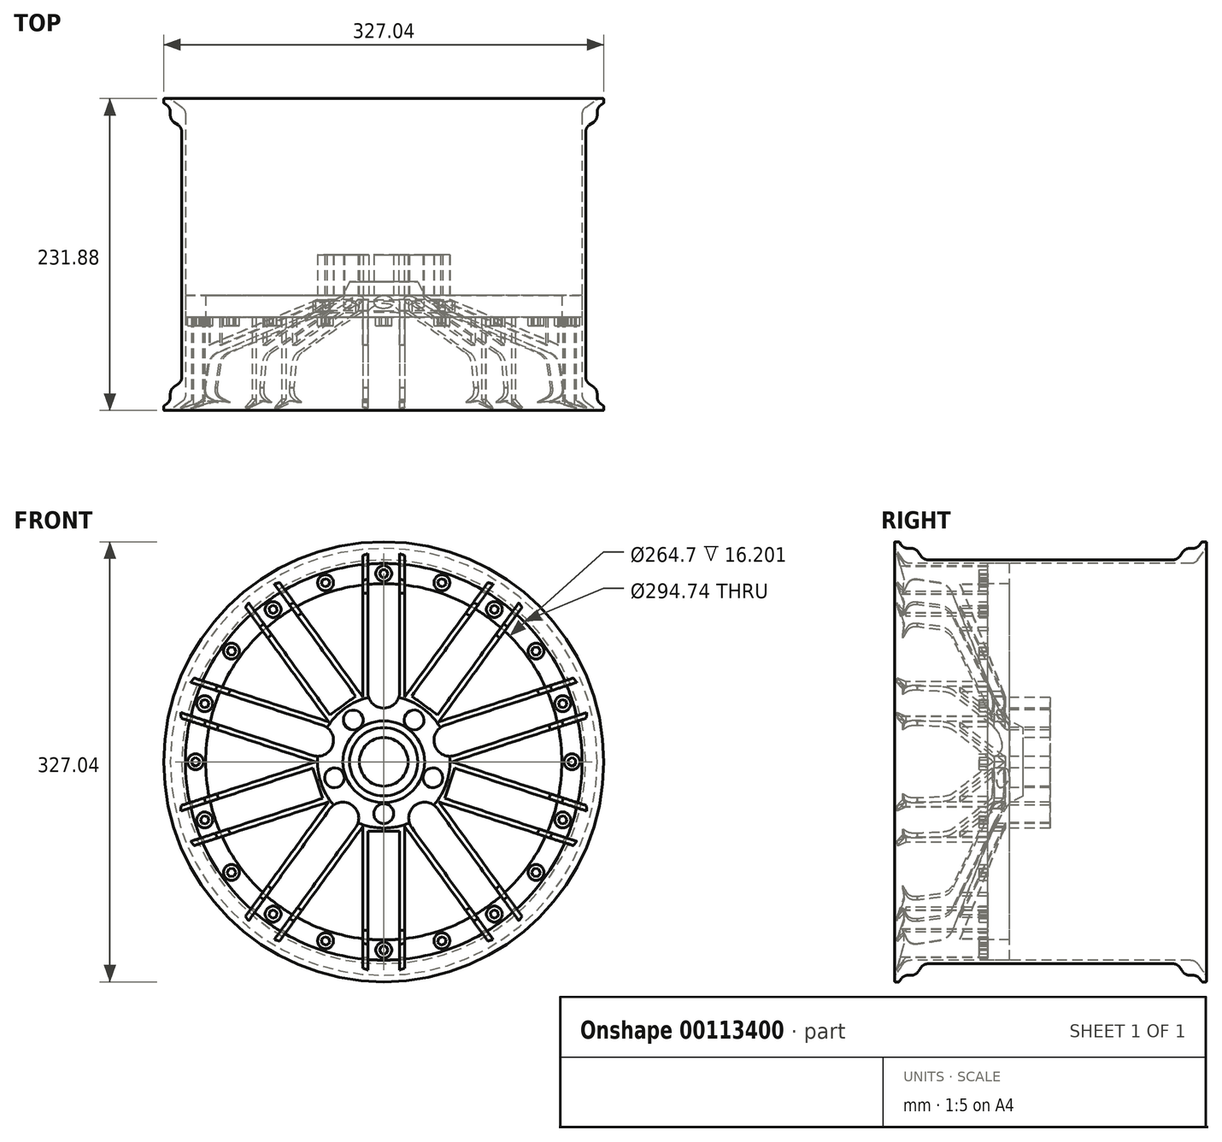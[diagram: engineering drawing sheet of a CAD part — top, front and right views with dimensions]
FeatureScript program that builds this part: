
annotation { "Feature Type Name" : "Feature", "Feature Type Description" : "" }
export const myFeature = defineFeature(function(context is Context, id is Id, definition is map)
    precondition{}
    {
        {
            var Q0;
            Q0=qCreatedBy(makeId("Right.planeOp"),FACE);
            var sketch = newSketch(context, id + "F0", { "sketchPlane" : qUnion([Q0])});
            skLineSegment(sketch, "E0", {"start": v(0, 0) * mm, "end": v(0, 25.37) * mm});
            skLineSegment(sketch, "E1", {"start": v(0, 25.37) * mm, "end": v(-9.97, 30.36) * mm});
            skLineSegment(sketch, "E2", {"start": v(-9.97, 30.36) * mm, "end": v(-21.68, 49.22) * mm});
            skLineSegment(sketch, "E3", {"start": v(-21.68, 49.22) * mm, "end": v(-52.6, 125.8) * mm});
            skLineSegment(sketch, "E4", {"start": v(-62.4, 133.6) * mm, "end": v(-78.7, 136.17) * mm});
            skLineSegment(sketch, "E5", {"start": v(-78.7, 136.17) * mm, "end": v(-80.6, 136.17) * mm});
            skLineSegment(sketch, "E6", {"start": v(-86.3, 132.6) * mm, "end": v(-89.55, 125.98) * mm});
            skLineSegment(sketch, "E7", {"start": v(-89.55, 125.98) * mm, "end": v(-88.47, 135.95) * mm});
            skLineSegment(sketch, "E8", {"start": v(-46.84, 132.48) * mm, "end": v(-13.23, 49.22) * mm});
            skLineSegment(sketch, "E9", {"start": v(-13.23, 49.22) * mm, "end": v(19.95, 49.22) * mm});
            skLineSegment(sketch, "E10", {"start": v(19.95, 49.22) * mm, "end": v(19.95, 0) * mm});
            skLineSegment(sketch, "E11", {"start": v(19.95, 0) * mm, "end": v(0, 0) * mm});
            skLineSegment(sketch, "E12", {"start": v(-46.84, 132.48) * mm, "end": v(-26.45, 132.48) * mm});
            skLineSegment(sketch, "E13", {"start": v(-26.45, 132.48) * mm, "end": v(-26.45, 145.93) * mm});
            skLineSegment(sketch, "E14", {"start": v(-26.45, 145.93) * mm, "end": v(-87.38, 145.93) * mm});
            skLineSegment(sketch, "E15", {"start": v(-40.33, 0) * mm, "end": v(58.54, 0) * mm});
            skLineSegment(sketch, "E16", {"start": v(-94.12, 155.55) * mm, "end": v(-88.47, 135.95) * mm});
            skLineSegment(sketch, "E17", {"start": v(-94.12, 155.55) * mm, "end": v(-87.38, 145.93) * mm});
            skPoint(sketch, "E18.visualSharp", {"position": v(-55.3, 132.48) * mm});
            skArc(sketch, "E18.filletArc", {"start": v(-55.17, 132.18) * mm, "mid": v(-55.35, 132.41) * mm, "end": v(-55.62, 132.53) * mm});
            skArc(sketch, "E19.filletArc", {"start": v(-52.6, 125.8) * mm, "mid": v(-56.47, 131) * mm, "end": v(-62.4, 133.6) * mm});
            skPoint(sketch, "E20.visualSharp", {"position": v(-84.56, 136.17) * mm});
            skArc(sketch, "E20.filletArc", {"start": v(-80.6, 136.17) * mm, "mid": v(-83.96, 135.2) * mm, "end": v(-86.3, 132.6) * mm});
            skSolve(sketch);
        }
        {
            var Q0;
            Q0 = qSketchRegion(id + "F0", true);
            var Q1;
            Q1=sQuery(id+"F0.wireOp",EDGE,"E15");
            revolve(context, id + "F1", {"entities" : qUnion([Q0]), "axis" : qUnion([Q1]), "revolveType" : RevolveType.FULL});
        }
        {
            var Q0;
            Q0=makeQuery(id+"F1.opRevolve","SWEPT_FACE",FACE,{"disambiguationData":[OSD([sQuery(id+"F0.wireOp",EDGE,"E0")])]});
            cPlane(context, id + "F2", {"entities" : qUnion([Q0]), "cplaneType" : CPlaneType.OFFSET, "offset" : 94.13 * mm, "width" : 152.4 * mm, "height" : 152.4 * mm});
        }
        {
            var Q0;
            Q0=qCreatedBy(id+"F2.planeOp",FACE);
            var sketch = newSketch(context, id + "F3", { "sketchPlane" : qUnion([Q0])});
            skCircle(sketch, "E21.cCircle", {"center": v(0, 0) * mm, "radius": 31.14 * mm, "construction": true});
            skPoint(sketch, "E21.0.midPoint", {"position": v(0, 31.14) * mm});
            skCircle(sketch, "E22", {"center": v(-22.63, 31.14) * mm, "radius": 7.35 * mm});
            skCircle(sketch, "E23", {"center": v(22.63, 31.14) * mm, "radius": 7.35 * mm});
            skCircle(sketch, "E24", {"center": v(36.61, -11.9) * mm, "radius": 7.35 * mm});
            skCircle(sketch, "E25", {"center": v(0, -38.5) * mm, "radius": 7.35 * mm});
            skCircle(sketch, "E26", {"center": v(-36.61, -11.9) * mm, "radius": 7.35 * mm});
            skCircle(sketch, "E27", {"center": v(0, 0) * mm, "radius": 18.07 * mm});
            skCircle(sketch, "E28.cCircle", {"center": v(0, 0) * mm, "radius": 48.17 * mm, "construction": true});
            skPoint(sketch, "E28.0.midPoint", {"position": v(0, -48.17) * mm});
            skLineSegment(sketch, "E29.left", {"start": v(15.65, -48.17) * mm, "end": v(15.65, -143.7) * mm});
            skLineSegment(sketch, "E29.right", {"start": v(-15.65, -48.17) * mm, "end": v(-15.65, -143.7) * mm});
            skLineSegment(sketch, "E30.bottom", {"start": v(11.83, -51.7) * mm, "end": v(-11.84, -51.7) * mm});
            skLineSegment(sketch, "E30.left", {"start": v(11.83, -51.7) * mm, "end": v(11.83, -145.13) * mm});
            skLineSegment(sketch, "E30.right", {"start": v(-11.84, -51.7) * mm, "end": v(-11.84, -145.13) * mm});
            skLineSegment(sketch, "E31.MirrorCS", {"start": v(-11.83, -145.13) * mm, "end": v(-11.84, -145.13) * mm});
            skPoint(sketch, "E32.orphan", {"position": v(-15.65, -149.28) * mm});
            skLineSegment(sketch, "E33.1.0", {"start": v(39.96, -34.87) * mm, "end": v(94.88, -110.46) * mm});
            skLineSegment(sketch, "E33.1.1", {"start": v(40.97, -29.77) * mm, "end": v(97.13, -107.06) * mm});
            skLineSegment(sketch, "E33.1.3", {"start": v(39.96, -34.87) * mm, "end": v(39.95, -34.87) * mm});
            skLineSegment(sketch, "E33.1.4", {"start": v(20.8, -48.78) * mm, "end": v(75.73, -124.37) * mm});
            skLineSegment(sketch, "E33.1.5", {"start": v(15.65, -48.17) * mm, "end": v(71.8, -125.46) * mm});
            skLineSegment(sketch, "E33.1.6", {"start": v(75.74, -124.37) * mm, "end": v(75.73, -124.37) * mm});
            skLineSegment(sketch, "E33.2.0", {"start": v(52.82, -4.72) * mm, "end": v(141.69, -33.6) * mm});
            skLineSegment(sketch, "E33.2.1", {"start": v(50.65, 0) * mm, "end": v(141.5, -29.52) * mm});
            skLineSegment(sketch, "E33.2.3", {"start": v(52.82, -4.72) * mm, "end": v(45.5, -27.23) * mm});
            skLineSegment(sketch, "E33.2.4", {"start": v(45.5, -27.23) * mm, "end": v(134.37, -56.1) * mm});
            skLineSegment(sketch, "E33.2.5", {"start": v(40.97, -29.77) * mm, "end": v(131.83, -59.3) * mm});
            skLineSegment(sketch, "E33.2.6", {"start": v(134.37, -56.1) * mm, "end": v(134.37, -56.1) * mm});
            skLineSegment(sketch, "E33.3.0", {"start": v(45.51, 27.23) * mm, "end": v(134.37, 56.1) * mm});
            skLineSegment(sketch, "E33.3.1", {"start": v(40.97, 29.77) * mm, "end": v(131.83, 59.3) * mm});
            skLineSegment(sketch, "E33.3.4", {"start": v(52.82, 4.72) * mm, "end": v(141.69, 33.59) * mm});
            skLineSegment(sketch, "E33.3.5", {"start": v(50.65, 0) * mm, "end": v(141.5, 29.52) * mm});
            skLineSegment(sketch, "E33.3.6", {"start": v(141.69, 33.6) * mm, "end": v(141.69, 33.59) * mm});
            skLineSegment(sketch, "E33.4.0", {"start": v(20.82, 48.78) * mm, "end": v(75.74, 124.37) * mm});
            skLineSegment(sketch, "E33.4.1", {"start": v(15.65, 48.17) * mm, "end": v(71.8, 125.46) * mm});
            skLineSegment(sketch, "E33.4.3", {"start": v(20.82, 48.78) * mm, "end": v(39.96, 34.87) * mm});
            skLineSegment(sketch, "E33.4.4", {"start": v(39.96, 34.87) * mm, "end": v(94.88, 110.46) * mm});
            skLineSegment(sketch, "E33.4.5", {"start": v(40.97, 29.77) * mm, "end": v(97.13, 107.06) * mm});
            skLineSegment(sketch, "E33.4.6", {"start": v(94.88, 110.46) * mm, "end": v(94.88, 110.46) * mm});
            skLineSegment(sketch, "E33.5.0", {"start": v(-11.83, 51.7) * mm, "end": v(-11.83, 145.13) * mm});
            skLineSegment(sketch, "E33.5.1", {"start": v(-15.65, 48.17) * mm, "end": v(-15.65, 143.7) * mm});
            skLineSegment(sketch, "E33.5.4", {"start": v(11.84, 51.7) * mm, "end": v(11.84, 145.13) * mm});
            skLineSegment(sketch, "E33.5.5", {"start": v(15.65, 48.17) * mm, "end": v(15.65, 143.7) * mm});
            skLineSegment(sketch, "E33.5.6", {"start": v(11.83, 145.13) * mm, "end": v(11.84, 145.13) * mm});
            skLineSegment(sketch, "E33.6.0", {"start": v(-39.96, 34.87) * mm, "end": v(-94.88, 110.46) * mm});
            skLineSegment(sketch, "E33.6.1", {"start": v(-40.97, 29.77) * mm, "end": v(-97.13, 107.06) * mm});
            skLineSegment(sketch, "E33.6.3", {"start": v(-39.96, 34.87) * mm, "end": v(-20.8, 48.78) * mm});
            skLineSegment(sketch, "E33.6.4", {"start": v(-20.8, 48.78) * mm, "end": v(-75.73, 124.37) * mm});
            skLineSegment(sketch, "E33.6.5", {"start": v(-15.65, 48.17) * mm, "end": v(-71.8, 125.46) * mm});
            skLineSegment(sketch, "E33.6.6", {"start": v(-75.74, 124.37) * mm, "end": v(-75.73, 124.37) * mm});
            skLineSegment(sketch, "E33.7.0", {"start": v(-52.82, 4.72) * mm, "end": v(-141.69, 33.6) * mm});
            skLineSegment(sketch, "E33.7.1", {"start": v(-50.65, 0) * mm, "end": v(-141.5, 29.52) * mm});
            skLineSegment(sketch, "E33.7.4", {"start": v(-45.5, 27.23) * mm, "end": v(-134.37, 56.1) * mm});
            skLineSegment(sketch, "E33.7.5", {"start": v(-40.97, 29.77) * mm, "end": v(-131.83, 59.3) * mm});
            skLineSegment(sketch, "E33.7.6", {"start": v(-134.37, 56.1) * mm, "end": v(-134.37, 56.1) * mm});
            skLineSegment(sketch, "E33.8.0", {"start": v(-45.51, -27.23) * mm, "end": v(-134.37, -56.1) * mm});
            skLineSegment(sketch, "E33.8.1", {"start": v(-40.97, -29.77) * mm, "end": v(-131.83, -59.3) * mm});
            skLineSegment(sketch, "E33.8.3", {"start": v(-45.51, -27.23) * mm, "end": v(-52.82, -4.72) * mm});
            skLineSegment(sketch, "E33.8.4", {"start": v(-52.82, -4.72) * mm, "end": v(-141.69, -33.59) * mm});
            skLineSegment(sketch, "E33.8.5", {"start": v(-50.65, 0) * mm, "end": v(-141.5, -29.52) * mm});
            skLineSegment(sketch, "E33.8.6", {"start": v(-141.69, -33.6) * mm, "end": v(-141.69, -33.59) * mm});
            skLineSegment(sketch, "E33.9.0", {"start": v(-20.82, -48.78) * mm, "end": v(-75.74, -124.37) * mm});
            skLineSegment(sketch, "E33.9.1", {"start": v(-15.65, -48.17) * mm, "end": v(-71.8, -125.46) * mm});
            skLineSegment(sketch, "E33.9.4", {"start": v(-39.96, -34.87) * mm, "end": v(-94.88, -110.46) * mm});
            skLineSegment(sketch, "E33.9.5", {"start": v(-40.97, -29.77) * mm, "end": v(-97.13, -107.06) * mm});
            skLineSegment(sketch, "E33.9.6", {"start": v(-94.88, -110.46) * mm, "end": v(-94.88, -110.46) * mm});
            skPoint(sketch, "E34.orphan", {"position": v(40.97, -29.77) * mm});
            skPoint(sketch, "E35.orphan", {"position": v(-15.65, -48.17) * mm});
            skPoint(sketch, "E36.orphan", {"position": v(-40.97, -29.77) * mm});
            skPoint(sketch, "E37.orphan", {"position": v(-50.65, 0) * mm});
            skPoint(sketch, "E38.orphan", {"position": v(-40.97, 29.77) * mm});
            skPoint(sketch, "E39.orphan", {"position": v(-15.65, 48.17) * mm});
            skPoint(sketch, "E40.orphan", {"position": v(15.65, 48.17) * mm});
            skArc(sketch, "E41", {"start": v(39.95, -34.87) * mm, "mid": v(23.43, -32.26) * mm, "end": v(20.82, -48.78) * mm});
            skArc(sketch, "E42", {"start": v(-21.05, -49.1) * mm, "mid": v(-23.43, -32.24) * mm, "end": v(-40.2, -35.2) * mm});
            skArc(sketch, "E43", {"start": v(-52.82, 4.72) * mm, "mid": v(-37.91, 12.32) * mm, "end": v(-45.5, 27.23) * mm});
            skArc(sketch, "E44", {"start": v(-11.83, 52.1) * mm, "mid": v(-0.2, 39.86) * mm, "end": v(11.84, 51.7) * mm});
            skArc(sketch, "E45", {"start": v(45.51, 27.23) * mm, "mid": v(37.91, 12.31) * mm, "end": v(52.82, 4.72) * mm});
            skLineSegment(sketch, "E46.trimOffspring", {"start": v(20.82, -48.78) * mm, "end": v(20.8, -48.78) * mm});
            skLineSegment(sketch, "E47", {"start": v(-15.65, 143.7) * mm, "end": v(-15.65, 153.27) * mm});
            skLineSegment(sketch, "E48", {"start": v(-15.65, 153.27) * mm, "end": v(-11.83, 154.7) * mm});
            skLineSegment(sketch, "E49", {"start": v(-11.83, 154.7) * mm, "end": v(-11.83, 145.13) * mm});
            skLineSegment(sketch, "E50.MirrorCS", {"start": v(11.83, 154.7) * mm, "end": v(11.83, 145.13) * mm});
            skLineSegment(sketch, "E51.MirrorCS", {"start": v(15.65, 153.27) * mm, "end": v(11.83, 154.7) * mm});
            skLineSegment(sketch, "E52.MirrorCS", {"start": v(15.65, 143.7) * mm, "end": v(15.65, 153.27) * mm});
            skLineSegment(sketch, "E53.1.0", {"start": v(-100.5, 118.2) * mm, "end": v(-94.88, 110.46) * mm});
            skLineSegment(sketch, "E53.1.1", {"start": v(-97.13, 107.06) * mm, "end": v(-102.75, 114.8) * mm});
            skLineSegment(sketch, "E53.1.2", {"start": v(-102.75, 114.8) * mm, "end": v(-100.5, 118.2) * mm});
            skLineSegment(sketch, "E53.1.3", {"start": v(-81.36, 132.1) * mm, "end": v(-75.74, 124.37) * mm});
            skLineSegment(sketch, "E53.1.4", {"start": v(-77.43, 133.2) * mm, "end": v(-81.36, 132.1) * mm});
            skLineSegment(sketch, "E53.1.5", {"start": v(-71.8, 125.46) * mm, "end": v(-77.43, 133.2) * mm});
            skLineSegment(sketch, "E53.2.0", {"start": v(-150.78, 36.55) * mm, "end": v(-141.69, 33.6) * mm});
            skLineSegment(sketch, "E53.2.1", {"start": v(-141.5, 29.52) * mm, "end": v(-150.6, 32.48) * mm});
            skLineSegment(sketch, "E53.2.2", {"start": v(-150.6, 32.48) * mm, "end": v(-150.78, 36.55) * mm});
            skLineSegment(sketch, "E53.2.3", {"start": v(-143.47, 59.06) * mm, "end": v(-134.37, 56.1) * mm});
            skLineSegment(sketch, "E53.2.4", {"start": v(-140.93, 62.25) * mm, "end": v(-143.47, 59.06) * mm});
            skLineSegment(sketch, "E53.2.5", {"start": v(-131.83, 59.3) * mm, "end": v(-140.93, 62.25) * mm});
            skLineSegment(sketch, "E53.3.0", {"start": v(-143.47, -59.06) * mm, "end": v(-134.37, -56.1) * mm});
            skLineSegment(sketch, "E53.3.1", {"start": v(-131.83, -59.3) * mm, "end": v(-140.93, -62.25) * mm});
            skLineSegment(sketch, "E53.3.2", {"start": v(-140.93, -62.25) * mm, "end": v(-143.47, -59.06) * mm});
            skLineSegment(sketch, "E53.3.3", {"start": v(-150.78, -36.55) * mm, "end": v(-141.69, -33.6) * mm});
            skLineSegment(sketch, "E53.3.4", {"start": v(-150.6, -32.48) * mm, "end": v(-150.78, -36.55) * mm});
            skLineSegment(sketch, "E53.3.5", {"start": v(-141.5, -29.52) * mm, "end": v(-150.6, -32.48) * mm});
            skLineSegment(sketch, "E53.4.0", {"start": v(-81.36, -132.1) * mm, "end": v(-75.74, -124.37) * mm});
            skLineSegment(sketch, "E53.4.1", {"start": v(-71.8, -125.46) * mm, "end": v(-77.43, -133.2) * mm});
            skLineSegment(sketch, "E53.4.2", {"start": v(-77.43, -133.2) * mm, "end": v(-81.36, -132.1) * mm});
            skLineSegment(sketch, "E53.4.3", {"start": v(-100.5, -118.2) * mm, "end": v(-94.88, -110.46) * mm});
            skLineSegment(sketch, "E53.4.4", {"start": v(-102.75, -114.8) * mm, "end": v(-100.5, -118.2) * mm});
            skLineSegment(sketch, "E53.4.5", {"start": v(-97.13, -107.06) * mm, "end": v(-102.75, -114.8) * mm});
            skLineSegment(sketch, "E53.5.0", {"start": v(11.83, -154.7) * mm, "end": v(11.83, -145.13) * mm});
            skLineSegment(sketch, "E53.5.1", {"start": v(15.65, -143.7) * mm, "end": v(15.65, -153.27) * mm});
            skLineSegment(sketch, "E53.5.2", {"start": v(15.65, -153.27) * mm, "end": v(11.83, -154.7) * mm});
            skLineSegment(sketch, "E53.5.3", {"start": v(-11.83, -154.7) * mm, "end": v(-11.83, -145.13) * mm});
            skLineSegment(sketch, "E53.5.4", {"start": v(-15.65, -153.27) * mm, "end": v(-11.83, -154.7) * mm});
            skLineSegment(sketch, "E53.5.5", {"start": v(-15.65, -143.7) * mm, "end": v(-15.65, -153.27) * mm});
            skLineSegment(sketch, "E53.6.0", {"start": v(100.5, -118.2) * mm, "end": v(94.88, -110.46) * mm});
            skLineSegment(sketch, "E53.6.1", {"start": v(97.13, -107.06) * mm, "end": v(102.75, -114.8) * mm});
            skLineSegment(sketch, "E53.6.2", {"start": v(102.75, -114.8) * mm, "end": v(100.5, -118.2) * mm});
            skLineSegment(sketch, "E53.6.3", {"start": v(81.36, -132.1) * mm, "end": v(75.74, -124.37) * mm});
            skLineSegment(sketch, "E53.6.4", {"start": v(77.43, -133.2) * mm, "end": v(81.36, -132.1) * mm});
            skLineSegment(sketch, "E53.6.5", {"start": v(71.8, -125.46) * mm, "end": v(77.43, -133.2) * mm});
            skLineSegment(sketch, "E53.7.0", {"start": v(150.78, -36.55) * mm, "end": v(141.69, -33.6) * mm});
            skLineSegment(sketch, "E53.7.1", {"start": v(141.5, -29.52) * mm, "end": v(150.6, -32.48) * mm});
            skLineSegment(sketch, "E53.7.2", {"start": v(150.6, -32.48) * mm, "end": v(150.78, -36.55) * mm});
            skLineSegment(sketch, "E53.7.3", {"start": v(143.47, -59.06) * mm, "end": v(134.37, -56.1) * mm});
            skLineSegment(sketch, "E53.7.4", {"start": v(140.93, -62.25) * mm, "end": v(143.47, -59.06) * mm});
            skLineSegment(sketch, "E53.7.5", {"start": v(131.83, -59.3) * mm, "end": v(140.93, -62.25) * mm});
            skLineSegment(sketch, "E53.8.0", {"start": v(143.47, 59.06) * mm, "end": v(134.37, 56.1) * mm});
            skLineSegment(sketch, "E53.8.1", {"start": v(131.83, 59.3) * mm, "end": v(140.93, 62.25) * mm});
            skLineSegment(sketch, "E53.8.2", {"start": v(140.93, 62.25) * mm, "end": v(143.47, 59.06) * mm});
            skLineSegment(sketch, "E53.8.3", {"start": v(150.78, 36.55) * mm, "end": v(141.69, 33.6) * mm});
            skLineSegment(sketch, "E53.8.4", {"start": v(150.6, 32.48) * mm, "end": v(150.78, 36.55) * mm});
            skLineSegment(sketch, "E53.8.5", {"start": v(141.5, 29.52) * mm, "end": v(150.6, 32.48) * mm});
            skLineSegment(sketch, "E53.9.0", {"start": v(81.36, 132.1) * mm, "end": v(75.74, 124.37) * mm});
            skLineSegment(sketch, "E53.9.1", {"start": v(71.8, 125.46) * mm, "end": v(77.43, 133.2) * mm});
            skLineSegment(sketch, "E53.9.2", {"start": v(77.43, 133.2) * mm, "end": v(81.36, 132.1) * mm});
            skLineSegment(sketch, "E53.9.3", {"start": v(100.5, 118.2) * mm, "end": v(94.88, 110.46) * mm});
            skLineSegment(sketch, "E53.9.4", {"start": v(102.75, 114.8) * mm, "end": v(100.5, 118.2) * mm});
            skLineSegment(sketch, "E53.9.5", {"start": v(97.13, 107.06) * mm, "end": v(102.75, 114.8) * mm});
            skPoint(sketch, "E54.start.orphan", {"position": v(0, 144.46) * mm});
            skSolve(sketch);
        }
        {
            var Q0;
            Q0 = qSketchRegion(id + "F3", true);
            extrude(context, id + "F4", {"entities" : qUnion([Q0]), "operationType" : NewBodyOperationType.INTERSECT, "endBound" : BoundingType.THROUGH_ALL, "oppositeDirection" : true, "depth" : 25.4 * mm});
        }
        {
            var Q0;
            Q0=qCreatedBy(makeId("Right.planeOp"),FACE);
            var sketch = newSketch(context, id + "F5", { "sketchPlane" : qUnion([Q0])});
            skLineSegment(sketch, "E55", {"start": v(-26.21, 147.37) * mm, "end": v(-83.99, 147.37) * mm});
            skLineSegment(sketch, "E56", {"start": v(-89.18, 150.06) * mm, "end": v(-94.53, 157.67) * mm});
            skLineSegment(sketch, "E57", {"start": v(-95.69, 161.33) * mm, "end": v(-95.69, 162.94) * mm});
            skPoint(sketch, "E58.visualSharp", {"position": v(-87.28, 147.37) * mm});
            skArc(sketch, "E58.filletArc", {"start": v(-89.18, 150.06) * mm, "mid": v(-86.91, 148.08) * mm, "end": v(-83.99, 147.37) * mm});
            skPoint(sketch, "E59.visualSharp", {"position": v(-95.69, 159.32) * mm});
            skArc(sketch, "E59.filletArc", {"start": v(-95.69, 161.33) * mm, "mid": v(-95.4, 159.41) * mm, "end": v(-94.53, 157.67) * mm});
            skLineSegment(sketch, "E60.MirrorCS", {"start": v(66.71, 147.37) * mm, "end": v(124.48, 147.37) * mm});
            skArc(sketch, "E61.MirrorCS", {"start": v(129.68, 150.06) * mm, "mid": v(127.41, 148.08) * mm, "end": v(124.48, 147.37) * mm});
            skLineSegment(sketch, "E62.MirrorCS", {"start": v(129.68, 150.06) * mm, "end": v(135.03, 157.67) * mm});
            skArc(sketch, "E63.MirrorCS", {"start": v(136.19, 161.33) * mm, "mid": v(135.9, 159.41) * mm, "end": v(135.03, 157.67) * mm});
            skLineSegment(sketch, "E64.MirrorCS", {"start": v(136.19, 161.33) * mm, "end": v(136.19, 162.94) * mm});
            skLineSegment(sketch, "E65", {"start": v(-26.21, 147.37) * mm, "end": v(66.71, 147.37) * mm});
            skLineSegment(sketch, "E66", {"start": v(20.25, 147.37) * mm, "end": v(20.25, 150.09) * mm});
            skLineSegment(sketch, "E67", {"start": v(20.25, 150.09) * mm, "end": v(111.22, 150.09) * mm});
            skLineSegment(sketch, "E68", {"start": v(116.47, 152.86) * mm, "end": v(118.5, 155.84) * mm});
            skLineSegment(sketch, "E69", {"start": v(123.75, 158.61) * mm, "end": v(126.07, 158.61) * mm});
            skLineSegment(sketch, "E70", {"start": v(131.23, 161.26) * mm, "end": v(132.68, 163.28) * mm});
            skLineSegment(sketch, "E71", {"start": v(133.15, 163.52) * mm, "end": v(135.6, 163.52) * mm});
            skPoint(sketch, "E72.visualSharp", {"position": v(114.58, 150.09) * mm});
            skArc(sketch, "E72.filletArc", {"start": v(111.22, 150.09) * mm, "mid": v(114.19, 150.82) * mm, "end": v(116.47, 152.86) * mm});
            skPoint(sketch, "E73.visualSharp", {"position": v(120.4, 158.61) * mm});
            skArc(sketch, "E73.filletArc", {"start": v(123.75, 158.61) * mm, "mid": v(120.79, 157.88) * mm, "end": v(118.5, 155.84) * mm});
            skPoint(sketch, "E74.visualSharp", {"position": v(129.33, 158.61) * mm});
            skArc(sketch, "E74.filletArc", {"start": v(126.07, 158.61) * mm, "mid": v(128.97, 159.32) * mm, "end": v(131.23, 161.26) * mm});
            skPoint(sketch, "E75.visualSharp", {"position": v(132.85, 163.52) * mm});
            skArc(sketch, "E75.filletArc", {"start": v(133.15, 163.52) * mm, "mid": v(132.88, 163.46) * mm, "end": v(132.68, 163.28) * mm});
            skPoint(sketch, "E76.visualSharp", {"position": v(136.19, 163.52) * mm});
            skArc(sketch, "E76.filletArc", {"start": v(136.19, 162.94) * mm, "mid": v(136.02, 163.35) * mm, "end": v(135.6, 163.52) * mm});
            skLineSegment(sketch, "E77.MirrorCS", {"start": v(20.25, 150.09) * mm, "end": v(-70.72, 150.09) * mm});
            skArc(sketch, "E78.MirrorCS", {"start": v(-70.72, 150.09) * mm, "mid": v(-73.69, 150.82) * mm, "end": v(-75.97, 152.86) * mm});
            skLineSegment(sketch, "E79.MirrorCS", {"start": v(-75.97, 152.86) * mm, "end": v(-78, 155.84) * mm});
            skArc(sketch, "E80.MirrorCS", {"start": v(-83.25, 158.61) * mm, "mid": v(-80.29, 157.88) * mm, "end": v(-78, 155.84) * mm});
            skLineSegment(sketch, "E81.MirrorCS", {"start": v(-83.25, 158.61) * mm, "end": v(-85.57, 158.61) * mm});
            skArc(sketch, "E82.MirrorCS", {"start": v(-85.57, 158.61) * mm, "mid": v(-88.47, 159.32) * mm, "end": v(-90.73, 161.26) * mm});
            skLineSegment(sketch, "E83.MirrorCS", {"start": v(-90.73, 161.26) * mm, "end": v(-92.18, 163.28) * mm});
            skLineSegment(sketch, "E84.MirrorCS", {"start": v(-92.65, 163.52) * mm, "end": v(-95.1, 163.52) * mm});
            skArc(sketch, "E85.MirrorCS", {"start": v(-95.69, 162.94) * mm, "mid": v(-95.52, 163.35) * mm, "end": v(-95.1, 163.52) * mm});
            skArc(sketch, "E86.MirrorCS", {"start": v(-92.65, 163.52) * mm, "mid": v(-92.38, 163.46) * mm, "end": v(-92.18, 163.28) * mm});
            skLineSegment(sketch, "E87", {"start": v(-40.11, 0) * mm, "end": v(59, 0) * mm});
            skSolve(sketch);
        }
        {
            var Q0;
            Q0 = qSketchRegion(id + "F5", true);
            var Q1;
            Q1=sQuery(id+"F5.wireOp",EDGE,"E87");
            revolve(context, id + "F6", {"entities" : qUnion([Q0]), "axis" : qUnion([Q1]), "revolveType" : RevolveType.FULL});
        }
        {
            var Q0;
            Q0=qCreatedBy(makeId("Right.planeOp"),FACE);
            var sketch = newSketch(context, id + "F7", { "sketchPlane" : qUnion([Q0])});
            skLineSegment(sketch, "E88", {"start": v(-26.44, 132.35) * mm, "end": v(-26.44, 147.42) * mm});
            skLineSegment(sketch, "E89", {"start": v(-26.44, 147.42) * mm, "end": v(-10.24, 147.42) * mm});
            skLineSegment(sketch, "E90", {"start": v(-10.24, 147.42) * mm, "end": v(-10.24, 132.35) * mm});
            skLineSegment(sketch, "E91", {"start": v(-10.24, 132.35) * mm, "end": v(-26.44, 132.35) * mm});
            skLineSegment(sketch, "E92", {"start": v(-39.1, 0) * mm, "end": v(58.45, 0) * mm});
            skSolve(sketch);
        }
        {
            var Q0;
            Q0 = qSketchRegion(id + "F7", true);
            var Q1;
            Q1=sQuery(id+"F7.wireOp",EDGE,"E92");
            revolve(context, id + "F8", {"entities" : qUnion([Q0]), "axis" : qUnion([Q1]), "revolveType" : RevolveType.FULL});
        }
        {
            var Q0;
            Q0=makeQuery(id+"F8.opRevolve","SWEPT_FACE",FACE,{"disambiguationData":[OSD([sQuery(id+"F7.wireOp",EDGE,"E88")])]});
            var sketch = newSketch(context, id + "F9", { "sketchPlane" : qUnion([Q0])});
            skCircle(sketch, "E93", {"center": v(0, 139.89) * mm, "radius": 5.92 * mm});
            skCircle(sketch, "E94.cCircle", {"center": v(0, 139.89) * mm, "radius": 2.8 * mm, "construction": true});
            skLineSegment(sketch, "E94.0", {"start": v(-1.61, 142.68) * mm, "end": v(1.61, 142.68) * mm});
            skLineSegment(sketch, "E94.1", {"start": v(1.61, 142.68) * mm, "end": v(3.22, 139.89) * mm});
            skLineSegment(sketch, "E94.2", {"start": v(3.22, 139.89) * mm, "end": v(1.61, 137.1) * mm});
            skLineSegment(sketch, "E94.3", {"start": v(1.61, 137.1) * mm, "end": v(-1.61, 137.1) * mm});
            skLineSegment(sketch, "E94.4", {"start": v(-1.61, 137.1) * mm, "end": v(-3.22, 139.89) * mm});
            skLineSegment(sketch, "E94.5", {"start": v(-3.22, 139.89) * mm, "end": v(-1.61, 142.68) * mm});
            skPoint(sketch, "E94.0.midPoint", {"position": v(0, 142.68) * mm});
            skPoint(sketch, "E95.orphan", {"position": v(0, 147.42) * mm});
            skPoint(sketch, "E96.orphan", {"position": v(0, 132.35) * mm});
            skCircle(sketch, "E97.1.0", {"center": v(-43.23, 133.04) * mm, "radius": 5.92 * mm});
            skLineSegment(sketch, "E97.1.1", {"start": v(-45.62, 135.2) * mm, "end": v(-42.56, 136.2) * mm});
            skLineSegment(sketch, "E97.1.2", {"start": v(-42.56, 136.2) * mm, "end": v(-40.16, 134.04) * mm});
            skLineSegment(sketch, "E97.1.3", {"start": v(-40.16, 134.04) * mm, "end": v(-40.83, 130.88) * mm});
            skLineSegment(sketch, "E97.1.4", {"start": v(-40.83, 130.88) * mm, "end": v(-43.9, 129.89) * mm});
            skLineSegment(sketch, "E97.1.5", {"start": v(-43.9, 129.89) * mm, "end": v(-46.3, 132.04) * mm});
            skLineSegment(sketch, "E97.1.6", {"start": v(-46.3, 132.04) * mm, "end": v(-45.62, 135.2) * mm});
            skCircle(sketch, "E97.2.0", {"center": v(-82.22, 113.17) * mm, "radius": 5.92 * mm});
            skLineSegment(sketch, "E97.2.1", {"start": v(-85.17, 114.48) * mm, "end": v(-82.56, 116.38) * mm});
            skLineSegment(sketch, "E97.2.2", {"start": v(-82.56, 116.38) * mm, "end": v(-79.62, 115.07) * mm});
            skLineSegment(sketch, "E97.2.3", {"start": v(-79.62, 115.07) * mm, "end": v(-79.28, 111.86) * mm});
            skLineSegment(sketch, "E97.2.4", {"start": v(-79.28, 111.86) * mm, "end": v(-81.89, 109.97) * mm});
            skLineSegment(sketch, "E97.2.5", {"start": v(-81.89, 109.97) * mm, "end": v(-84.83, 111.28) * mm});
            skLineSegment(sketch, "E97.2.6", {"start": v(-84.83, 111.28) * mm, "end": v(-85.17, 114.48) * mm});
            skCircle(sketch, "E97.3.0", {"center": v(-113.17, 82.22) * mm, "radius": 5.92 * mm});
            skLineSegment(sketch, "E97.3.1", {"start": v(-116.38, 82.56) * mm, "end": v(-114.48, 85.17) * mm});
            skLineSegment(sketch, "E97.3.2", {"start": v(-114.48, 85.17) * mm, "end": v(-111.28, 84.83) * mm});
            skLineSegment(sketch, "E97.3.3", {"start": v(-111.28, 84.83) * mm, "end": v(-109.97, 81.89) * mm});
            skLineSegment(sketch, "E97.3.4", {"start": v(-109.97, 81.89) * mm, "end": v(-111.86, 79.28) * mm});
            skLineSegment(sketch, "E97.3.5", {"start": v(-111.86, 79.28) * mm, "end": v(-115.07, 79.62) * mm});
            skLineSegment(sketch, "E97.3.6", {"start": v(-115.07, 79.62) * mm, "end": v(-116.38, 82.56) * mm});
            skCircle(sketch, "E97.4.0", {"center": v(-133.04, 43.23) * mm, "radius": 5.92 * mm});
            skLineSegment(sketch, "E97.4.1", {"start": v(-136.2, 42.56) * mm, "end": v(-135.2, 45.62) * mm});
            skLineSegment(sketch, "E97.4.2", {"start": v(-135.2, 45.62) * mm, "end": v(-132.04, 46.3) * mm});
            skLineSegment(sketch, "E97.4.3", {"start": v(-132.04, 46.3) * mm, "end": v(-129.89, 43.9) * mm});
            skLineSegment(sketch, "E97.4.4", {"start": v(-129.89, 43.9) * mm, "end": v(-130.88, 40.83) * mm});
            skLineSegment(sketch, "E97.4.5", {"start": v(-130.88, 40.83) * mm, "end": v(-134.04, 40.16) * mm});
            skLineSegment(sketch, "E97.4.6", {"start": v(-134.04, 40.16) * mm, "end": v(-136.2, 42.56) * mm});
            skCircle(sketch, "E97.5.0", {"center": v(-139.89, 0) * mm, "radius": 5.92 * mm});
            skLineSegment(sketch, "E97.5.1", {"start": v(-142.68, -1.61) * mm, "end": v(-142.68, 1.61) * mm});
            skLineSegment(sketch, "E97.5.2", {"start": v(-142.68, 1.61) * mm, "end": v(-139.89, 3.22) * mm});
            skLineSegment(sketch, "E97.5.3", {"start": v(-139.89, 3.22) * mm, "end": v(-137.1, 1.61) * mm});
            skLineSegment(sketch, "E97.5.4", {"start": v(-137.1, 1.61) * mm, "end": v(-137.1, -1.61) * mm});
            skLineSegment(sketch, "E97.5.5", {"start": v(-137.1, -1.61) * mm, "end": v(-139.89, -3.22) * mm});
            skLineSegment(sketch, "E97.5.6", {"start": v(-139.89, -3.22) * mm, "end": v(-142.68, -1.61) * mm});
            skCircle(sketch, "E97.6.0", {"center": v(-133.04, -43.23) * mm, "radius": 5.92 * mm});
            skLineSegment(sketch, "E97.6.1", {"start": v(-135.2, -45.62) * mm, "end": v(-136.2, -42.56) * mm});
            skLineSegment(sketch, "E97.6.2", {"start": v(-136.2, -42.56) * mm, "end": v(-134.04, -40.16) * mm});
            skLineSegment(sketch, "E97.6.3", {"start": v(-134.04, -40.16) * mm, "end": v(-130.88, -40.83) * mm});
            skLineSegment(sketch, "E97.6.4", {"start": v(-130.88, -40.83) * mm, "end": v(-129.89, -43.9) * mm});
            skLineSegment(sketch, "E97.6.5", {"start": v(-129.89, -43.9) * mm, "end": v(-132.04, -46.3) * mm});
            skLineSegment(sketch, "E97.6.6", {"start": v(-132.04, -46.3) * mm, "end": v(-135.2, -45.62) * mm});
            skCircle(sketch, "E97.7.0", {"center": v(-113.17, -82.22) * mm, "radius": 5.92 * mm});
            skLineSegment(sketch, "E97.7.1", {"start": v(-114.48, -85.17) * mm, "end": v(-116.38, -82.56) * mm});
            skLineSegment(sketch, "E97.7.2", {"start": v(-116.38, -82.56) * mm, "end": v(-115.07, -79.62) * mm});
            skLineSegment(sketch, "E97.7.3", {"start": v(-115.07, -79.62) * mm, "end": v(-111.86, -79.28) * mm});
            skLineSegment(sketch, "E97.7.4", {"start": v(-111.86, -79.28) * mm, "end": v(-109.97, -81.89) * mm});
            skLineSegment(sketch, "E97.7.5", {"start": v(-109.97, -81.89) * mm, "end": v(-111.28, -84.83) * mm});
            skLineSegment(sketch, "E97.7.6", {"start": v(-111.28, -84.83) * mm, "end": v(-114.48, -85.17) * mm});
            skCircle(sketch, "E97.8.0", {"center": v(-82.22, -113.17) * mm, "radius": 5.92 * mm});
            skLineSegment(sketch, "E97.8.1", {"start": v(-82.56, -116.38) * mm, "end": v(-85.17, -114.48) * mm});
            skLineSegment(sketch, "E97.8.2", {"start": v(-85.17, -114.48) * mm, "end": v(-84.83, -111.28) * mm});
            skLineSegment(sketch, "E97.8.3", {"start": v(-84.83, -111.28) * mm, "end": v(-81.89, -109.97) * mm});
            skLineSegment(sketch, "E97.8.4", {"start": v(-81.89, -109.97) * mm, "end": v(-79.28, -111.86) * mm});
            skLineSegment(sketch, "E97.8.5", {"start": v(-79.28, -111.86) * mm, "end": v(-79.62, -115.07) * mm});
            skLineSegment(sketch, "E97.8.6", {"start": v(-79.62, -115.07) * mm, "end": v(-82.56, -116.38) * mm});
            skCircle(sketch, "E97.9.0", {"center": v(-43.23, -133.04) * mm, "radius": 5.92 * mm});
            skLineSegment(sketch, "E97.9.1", {"start": v(-42.56, -136.2) * mm, "end": v(-45.62, -135.2) * mm});
            skLineSegment(sketch, "E97.9.2", {"start": v(-45.62, -135.2) * mm, "end": v(-46.3, -132.04) * mm});
            skLineSegment(sketch, "E97.9.3", {"start": v(-46.3, -132.04) * mm, "end": v(-43.9, -129.89) * mm});
            skLineSegment(sketch, "E97.9.4", {"start": v(-43.9, -129.89) * mm, "end": v(-40.83, -130.88) * mm});
            skLineSegment(sketch, "E97.9.5", {"start": v(-40.83, -130.88) * mm, "end": v(-40.16, -134.04) * mm});
            skLineSegment(sketch, "E97.9.6", {"start": v(-40.16, -134.04) * mm, "end": v(-42.56, -136.2) * mm});
            skCircle(sketch, "E97.10.0", {"center": v(0, -139.89) * mm, "radius": 5.92 * mm});
            skLineSegment(sketch, "E97.10.1", {"start": v(1.61, -142.68) * mm, "end": v(-1.61, -142.68) * mm});
            skLineSegment(sketch, "E97.10.2", {"start": v(-1.61, -142.68) * mm, "end": v(-3.22, -139.89) * mm});
            skLineSegment(sketch, "E97.10.3", {"start": v(-3.22, -139.89) * mm, "end": v(-1.61, -137.1) * mm});
            skLineSegment(sketch, "E97.10.4", {"start": v(-1.61, -137.1) * mm, "end": v(1.61, -137.1) * mm});
            skLineSegment(sketch, "E97.10.5", {"start": v(1.61, -137.1) * mm, "end": v(3.22, -139.89) * mm});
            skLineSegment(sketch, "E97.10.6", {"start": v(3.22, -139.89) * mm, "end": v(1.61, -142.68) * mm});
            skCircle(sketch, "E97.11.0", {"center": v(43.23, -133.04) * mm, "radius": 5.92 * mm});
            skLineSegment(sketch, "E97.11.1", {"start": v(45.62, -135.2) * mm, "end": v(42.56, -136.2) * mm});
            skLineSegment(sketch, "E97.11.2", {"start": v(42.56, -136.2) * mm, "end": v(40.16, -134.04) * mm});
            skLineSegment(sketch, "E97.11.3", {"start": v(40.16, -134.04) * mm, "end": v(40.83, -130.88) * mm});
            skLineSegment(sketch, "E97.11.4", {"start": v(40.83, -130.88) * mm, "end": v(43.9, -129.89) * mm});
            skLineSegment(sketch, "E97.11.5", {"start": v(43.9, -129.89) * mm, "end": v(46.3, -132.04) * mm});
            skLineSegment(sketch, "E97.11.6", {"start": v(46.3, -132.04) * mm, "end": v(45.62, -135.2) * mm});
            skCircle(sketch, "E97.12.0", {"center": v(82.22, -113.17) * mm, "radius": 5.92 * mm});
            skLineSegment(sketch, "E97.12.1", {"start": v(85.17, -114.48) * mm, "end": v(82.56, -116.38) * mm});
            skLineSegment(sketch, "E97.12.2", {"start": v(82.56, -116.38) * mm, "end": v(79.62, -115.07) * mm});
            skLineSegment(sketch, "E97.12.3", {"start": v(79.62, -115.07) * mm, "end": v(79.28, -111.86) * mm});
            skLineSegment(sketch, "E97.12.4", {"start": v(79.28, -111.86) * mm, "end": v(81.89, -109.97) * mm});
            skLineSegment(sketch, "E97.12.5", {"start": v(81.89, -109.97) * mm, "end": v(84.83, -111.28) * mm});
            skLineSegment(sketch, "E97.12.6", {"start": v(84.83, -111.28) * mm, "end": v(85.17, -114.48) * mm});
            skCircle(sketch, "E97.13.0", {"center": v(113.17, -82.22) * mm, "radius": 5.92 * mm});
            skLineSegment(sketch, "E97.13.1", {"start": v(116.38, -82.56) * mm, "end": v(114.48, -85.17) * mm});
            skLineSegment(sketch, "E97.13.2", {"start": v(114.48, -85.17) * mm, "end": v(111.28, -84.83) * mm});
            skLineSegment(sketch, "E97.13.3", {"start": v(111.28, -84.83) * mm, "end": v(109.97, -81.89) * mm});
            skLineSegment(sketch, "E97.13.4", {"start": v(109.97, -81.89) * mm, "end": v(111.86, -79.28) * mm});
            skLineSegment(sketch, "E97.13.5", {"start": v(111.86, -79.28) * mm, "end": v(115.07, -79.62) * mm});
            skLineSegment(sketch, "E97.13.6", {"start": v(115.07, -79.62) * mm, "end": v(116.38, -82.56) * mm});
            skCircle(sketch, "E97.14.0", {"center": v(133.04, -43.23) * mm, "radius": 5.92 * mm});
            skLineSegment(sketch, "E97.14.1", {"start": v(136.2, -42.56) * mm, "end": v(135.2, -45.62) * mm});
            skLineSegment(sketch, "E97.14.2", {"start": v(135.2, -45.62) * mm, "end": v(132.04, -46.3) * mm});
            skLineSegment(sketch, "E97.14.3", {"start": v(132.04, -46.3) * mm, "end": v(129.89, -43.9) * mm});
            skLineSegment(sketch, "E97.14.4", {"start": v(129.89, -43.9) * mm, "end": v(130.88, -40.83) * mm});
            skLineSegment(sketch, "E97.14.5", {"start": v(130.88, -40.83) * mm, "end": v(134.04, -40.16) * mm});
            skLineSegment(sketch, "E97.14.6", {"start": v(134.04, -40.16) * mm, "end": v(136.2, -42.56) * mm});
            skCircle(sketch, "E97.15.0", {"center": v(139.89, 0) * mm, "radius": 5.92 * mm});
            skLineSegment(sketch, "E97.15.1", {"start": v(142.68, 1.61) * mm, "end": v(142.68, -1.61) * mm});
            skLineSegment(sketch, "E97.15.2", {"start": v(142.68, -1.61) * mm, "end": v(139.89, -3.22) * mm});
            skLineSegment(sketch, "E97.15.3", {"start": v(139.89, -3.22) * mm, "end": v(137.1, -1.61) * mm});
            skLineSegment(sketch, "E97.15.4", {"start": v(137.1, -1.61) * mm, "end": v(137.1, 1.61) * mm});
            skLineSegment(sketch, "E97.15.5", {"start": v(137.1, 1.61) * mm, "end": v(139.89, 3.22) * mm});
            skLineSegment(sketch, "E97.15.6", {"start": v(139.89, 3.22) * mm, "end": v(142.68, 1.61) * mm});
            skCircle(sketch, "E97.16.0", {"center": v(133.04, 43.23) * mm, "radius": 5.92 * mm});
            skLineSegment(sketch, "E97.16.1", {"start": v(135.2, 45.62) * mm, "end": v(136.2, 42.56) * mm});
            skLineSegment(sketch, "E97.16.2", {"start": v(136.2, 42.56) * mm, "end": v(134.04, 40.16) * mm});
            skLineSegment(sketch, "E97.16.3", {"start": v(134.04, 40.16) * mm, "end": v(130.88, 40.83) * mm});
            skLineSegment(sketch, "E97.16.4", {"start": v(130.88, 40.83) * mm, "end": v(129.89, 43.9) * mm});
            skLineSegment(sketch, "E97.16.5", {"start": v(129.89, 43.9) * mm, "end": v(132.04, 46.3) * mm});
            skLineSegment(sketch, "E97.16.6", {"start": v(132.04, 46.3) * mm, "end": v(135.2, 45.62) * mm});
            skCircle(sketch, "E97.17.0", {"center": v(113.17, 82.22) * mm, "radius": 5.92 * mm});
            skLineSegment(sketch, "E97.17.1", {"start": v(114.48, 85.17) * mm, "end": v(116.38, 82.56) * mm});
            skLineSegment(sketch, "E97.17.2", {"start": v(116.38, 82.56) * mm, "end": v(115.07, 79.62) * mm});
            skLineSegment(sketch, "E97.17.3", {"start": v(115.07, 79.62) * mm, "end": v(111.86, 79.28) * mm});
            skLineSegment(sketch, "E97.17.4", {"start": v(111.86, 79.28) * mm, "end": v(109.97, 81.89) * mm});
            skLineSegment(sketch, "E97.17.5", {"start": v(109.97, 81.89) * mm, "end": v(111.28, 84.83) * mm});
            skLineSegment(sketch, "E97.17.6", {"start": v(111.28, 84.83) * mm, "end": v(114.48, 85.17) * mm});
            skCircle(sketch, "E97.18.0", {"center": v(82.22, 113.17) * mm, "radius": 5.92 * mm});
            skLineSegment(sketch, "E97.18.1", {"start": v(82.56, 116.38) * mm, "end": v(85.17, 114.48) * mm});
            skLineSegment(sketch, "E97.18.2", {"start": v(85.17, 114.48) * mm, "end": v(84.83, 111.28) * mm});
            skLineSegment(sketch, "E97.18.3", {"start": v(84.83, 111.28) * mm, "end": v(81.89, 109.97) * mm});
            skLineSegment(sketch, "E97.18.4", {"start": v(81.89, 109.97) * mm, "end": v(79.28, 111.86) * mm});
            skLineSegment(sketch, "E97.18.5", {"start": v(79.28, 111.86) * mm, "end": v(79.62, 115.07) * mm});
            skLineSegment(sketch, "E97.18.6", {"start": v(79.62, 115.07) * mm, "end": v(82.56, 116.38) * mm});
            skCircle(sketch, "E97.19.0", {"center": v(43.23, 133.04) * mm, "radius": 5.92 * mm});
            skLineSegment(sketch, "E97.19.1", {"start": v(42.56, 136.2) * mm, "end": v(45.62, 135.2) * mm});
            skLineSegment(sketch, "E97.19.2", {"start": v(45.62, 135.2) * mm, "end": v(46.3, 132.04) * mm});
            skLineSegment(sketch, "E97.19.3", {"start": v(46.3, 132.04) * mm, "end": v(43.9, 129.89) * mm});
            skLineSegment(sketch, "E97.19.4", {"start": v(43.9, 129.89) * mm, "end": v(40.83, 130.88) * mm});
            skLineSegment(sketch, "E97.19.5", {"start": v(40.83, 130.88) * mm, "end": v(40.16, 134.04) * mm});
            skLineSegment(sketch, "E97.19.6", {"start": v(40.16, 134.04) * mm, "end": v(42.56, 136.2) * mm});
            skPoint(sketch, "E97.center", {"position": v(0, 0) * mm});
            skSolve(sketch);
        }
        {
            var Q0;
            Q0 = qSketchRegion(id + "F9", true);
            extrude(context, id + "F10", {"entities" : qUnion([Q0]), "depth" : 6.35 * mm});
        }
    });
